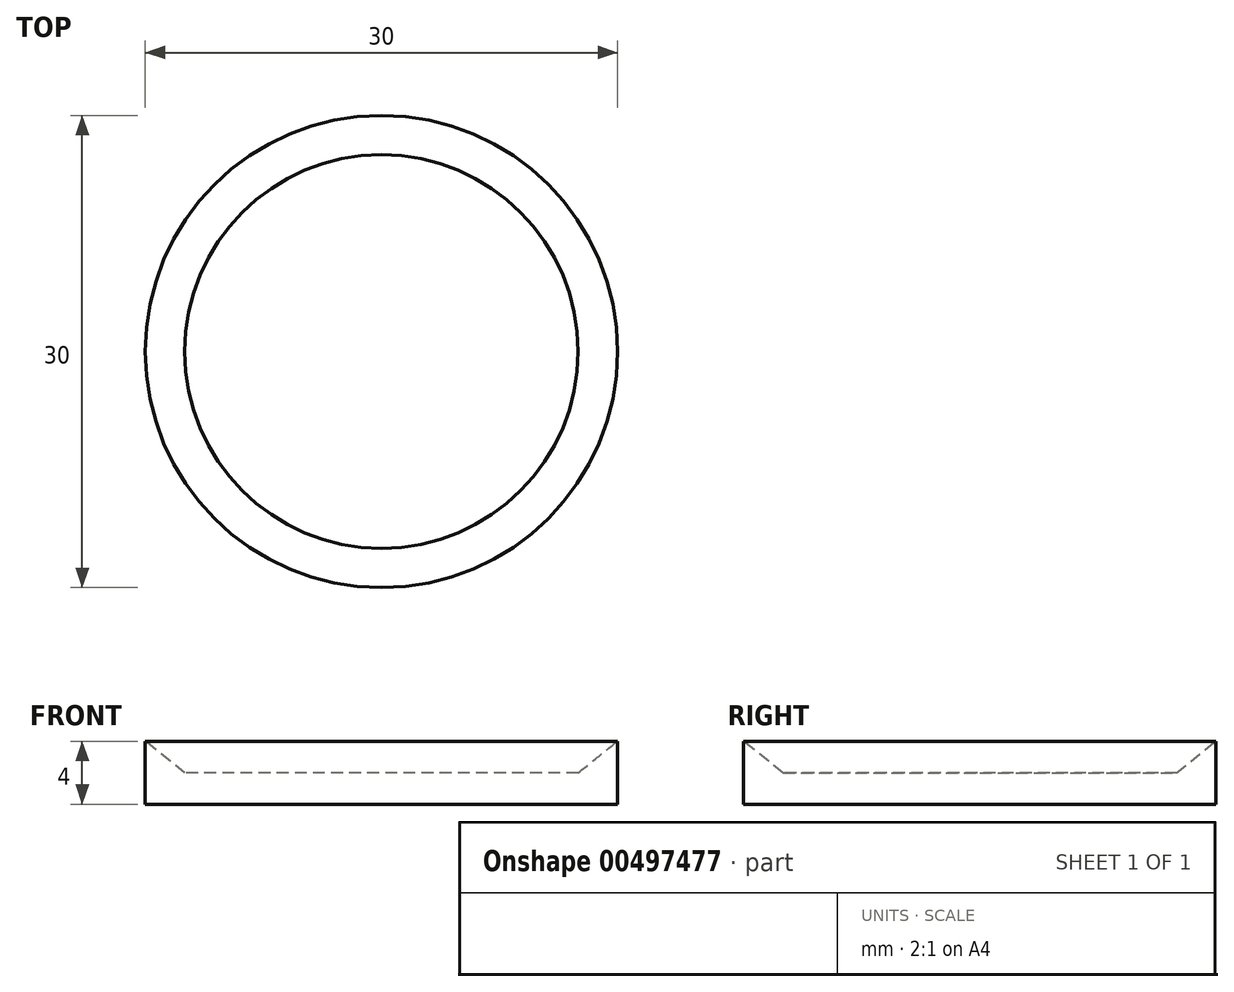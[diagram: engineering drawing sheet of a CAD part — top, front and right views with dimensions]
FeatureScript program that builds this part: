
annotation { "Feature Type Name" : "Feature", "Feature Type Description" : "" }
export const myFeature = defineFeature(function(context is Context, id is Id, definition is map)
    precondition{}
    {
        {
            var Q0;
            Q0=qCreatedBy(makeId("Front.planeOp"),FACE);
            var sketch = newSketch(context, id + "F0", { "sketchPlane" : qUnion([Q0])});
            skLineSegment(sketch, "E0", {"start": v(0, 82.14) * mm, "end": v(0, -83.49) * mm, "construction": true});
            skLineSegment(sketch, "E1", {"start": v(0, 0) * mm, "end": v(0, 2) * mm});
            skLineSegment(sketch, "E2", {"start": v(0, 2) * mm, "end": v(12.5, 2) * mm});
            skLineSegment(sketch, "E3", {"start": v(12.5, 2) * mm, "end": v(15, 4) * mm});
            skLineSegment(sketch, "E4", {"start": v(15, 4) * mm, "end": v(15, 0) * mm});
            skLineSegment(sketch, "E5", {"start": v(15, 0) * mm, "end": v(0, 0) * mm});
            skSolve(sketch);
        }
        {
            var Q0;
            Q0=makeQuery(id+"F0.imprint","IMPRINT",FACE,{"disambiguationData":[TD([[makeQuery(id+"F0.imprint","IMPRINT",EDGE,{"derivedFrom":sQuery(id+"F0.wireOp",EDGE,"E1")}),-1.0]])]});
            var Q1;
            Q1=sQuery(id+"F0.wireOp",EDGE,"E0");
            revolve(context, id + "F1", {"entities" : qUnion([Q0]), "axis" : qUnion([Q1]), "revolveType" : RevolveType.FULL});
        }
    });
